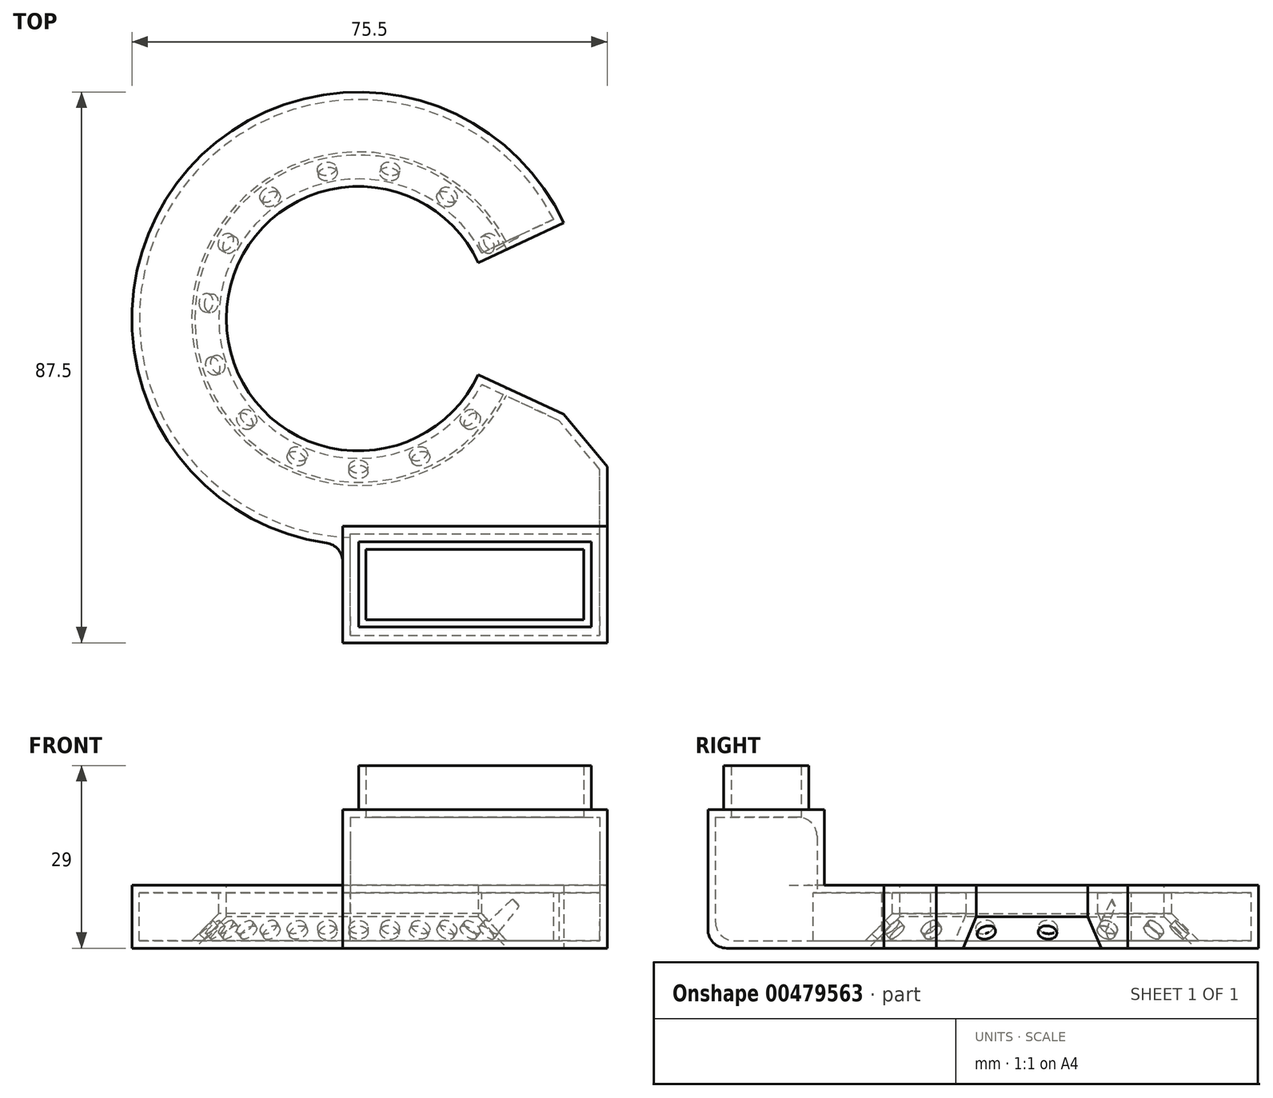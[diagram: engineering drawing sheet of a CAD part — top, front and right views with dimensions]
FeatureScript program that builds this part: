
annotation { "Feature Type Name" : "Feature", "Feature Type Description" : "" }
export const myFeature = defineFeature(function(context is Context, id is Id, definition is map)
    precondition{}
    {
        {
            var Q0;
            Q0=qCreatedBy(makeId("Front.planeOp"),FACE);
            var sketch = newSketch(context, id + "F0", { "sketchPlane" : qUnion([Q0])});
            skLineSegment(sketch, "E0", {"start": v(0, 66.2) * mm, "end": v(0, -56.66) * mm, "construction": true});
            skLineSegment(sketch, "E1", {"start": v(21, 10) * mm, "end": v(36, 10) * mm});
            skLineSegment(sketch, "E2", {"start": v(36, 10) * mm, "end": v(36, 0) * mm});
            skLineSegment(sketch, "E3", {"start": v(36, 0) * mm, "end": v(26, 0) * mm});
            skLineSegment(sketch, "E4", {"start": v(21, 10) * mm, "end": v(21, 5) * mm});
            skLineSegment(sketch, "E5", {"start": v(21, 5) * mm, "end": v(26, 0) * mm});
            skSolve(sketch);
        }
        {
            var Q0;
            Q0=makeQuery(id+"F0.imprint","IMPRINT",FACE,{"disambiguationData":[TD([[makeQuery(id+"F0.imprint","IMPRINT",EDGE,{"derivedFrom":sQuery(id+"F0.wireOp",EDGE,"E1")}),-1.0]])]});
            var Q1;
            Q1=sQuery(id+"F0.wireOp",EDGE,"E0");
            revolve(context, id + "F1", {"entities" : qUnion([Q0]), "axis" : qUnion([Q1]), "revolveType" : RevolveType.TWO_DIRECTIONS, "angle" : 335 * degree, "angleBack" : 25 * degree});
        }
        {
            var Q0;
            Q0=qCreatedBy(makeId("Top.planeOp"),FACE);
            var sketch = newSketch(context, id + "F2", { "sketchPlane" : qUnion([Q0])});
            skLineSegment(sketch, "E6.bottom", {"start": v(-2.5, -51.5) * mm, "end": v(39.5, -51.5) * mm});
            skLineSegment(sketch, "E6.left", {"start": v(-2.5, -51.5) * mm, "end": v(-2.5, -31.44) * mm});
            skLineSegment(sketch, "E6.right", {"start": v(39.5, -51.5) * mm, "end": v(39.5, -23.5) * mm});
            skPoint(sketch, "E7.orphan", {"position": v(23.56, -10.99) * mm});
            skPoint(sketch, "E8.orphan", {"position": v(23.56, 10.99) * mm});
            skPoint(sketch, "E9.0", {"position": v(32.63, -15.21) * mm});
            skLineSegment(sketch, "E10", {"start": v(39.5, -23.5) * mm, "end": v(32.63, -15.21) * mm});
            skLineSegment(sketch, "E11", {"start": v(32.63, -15.21) * mm, "end": v(-2.5, -31.44) * mm});
            skSolve(sketch);
        }
        {
            var Q0;
            Q0=makeQuery(id+"F2.imprint","IMPRINT",FACE,{"disambiguationData":[TD([[makeQuery(id+"F2.imprint","IMPRINT",EDGE,{"derivedFrom":sQuery(id+"F2.wireOp",EDGE,"E6.bottom")}),1.0]])]});
            var Q1;
            Q1=makeQuery(id+"F1.opRevolve","SWEPT_FACE",FACE,{"disambiguationData":[OSD([sQuery(id+"F0.wireOp",EDGE,"E1")])]});
            extrude(context, id + "F3", {"entities" : qUnion([Q0]), "operationType" : NewBodyOperationType.ADD, "endBound" : BoundingType.UP_TO_SURFACE, "endBoundEntityFace" : qUnion([Q1]), "depth" : 25 * mm});
        }
        {
            var Q0;
            {var subQ0=sQuery(id+"F0.wireOp",EDGE,"E1");Q0=makeQuery(id+"F3.boolean.opBoolean","MERGE",FACE,{"derivedFrom":[makeQuery(id+"F1.opRevolve","SWEPT_FACE",FACE,{"disambiguationData":[OSD([subQ0])]}),makeQuery(id+"F3.opExtrude","CAP_FACE",FACE,{"disambiguationData":[OSD([subQ0])],"isStart":false})]});}
            var sketch = newSketch(context, id + "F4", { "sketchPlane" : qUnion([Q0])});
            skPoint(sketch, "E12.0", {"position": v(-2.5, -51.5) * mm});
            skLineSegment(sketch, "E13.bottom", {"start": v(-2.5, -51.5) * mm, "end": v(39.5, -51.5) * mm});
            skLineSegment(sketch, "E13.top", {"start": v(-2.5, -32.96) * mm, "end": v(39.5, -32.96) * mm});
            skLineSegment(sketch, "E13.left", {"start": v(-2.5, -51.5) * mm, "end": v(-2.5, -32.96) * mm});
            skLineSegment(sketch, "E13.right", {"start": v(39.5, -51.5) * mm, "end": v(39.5, -32.96) * mm});
            skSolve(sketch);
        }
        {
            var Q0;
            Q0=makeQuery(id+"F4.imprint","IMPRINT",FACE,{"disambiguationData":[TD([[makeQuery(id+"F4.imprint","IMPRINT",EDGE,{"derivedFrom":sQuery(id+"F4.wireOp",EDGE,"E13.bottom")}),1.0]])]});
            extrude(context, id + "F5", {"entities" : qUnion([Q0]), "operationType" : NewBodyOperationType.ADD, "depth" : 12 * mm});
        }
        {
            var Q0;
            Q0=makeQuery(id+"F5.opExtrude","CAP_FACE",FACE,{"disambiguationData":[OSD([sQuery(id+"F4.wireOp",EDGE,"E13.bottom"),sQuery(id+"F4.wireOp",EDGE,"E13.top"),sQuery(id+"F4.wireOp",EDGE,"E13.left"),sQuery(id+"F4.wireOp",EDGE,"E13.right")])],"isStart":false});
            var sketch = newSketch(context, id + "F6", { "sketchPlane" : qUnion([Q0])});
            skPoint(sketch, "E14.0", {"position": v(-2.5, -32.96) * mm});
            skPoint(sketch, "E15.0", {"position": v(-2.5, -51.5) * mm});
            skPoint(sketch, "E16.0", {"position": v(39.5, -51.5) * mm});
            skPoint(sketch, "E17.0", {"position": v(39.5, -32.96) * mm});
            skLineSegment(sketch, "E18", {"start": v(-2.5, -32.96) * mm, "end": v(39.5, -51.5) * mm, "construction": true});
            skLineSegment(sketch, "E19", {"start": v(-2.5, -51.5) * mm, "end": v(39.5, -32.96) * mm, "construction": true});
            skLineSegment(sketch, "E20.bottom", {"start": v(37, -35.46) * mm, "end": v(0, -35.46) * mm});
            skLineSegment(sketch, "E20.top", {"start": v(37, -49) * mm, "end": v(0, -49) * mm});
            skLineSegment(sketch, "E20.left", {"start": v(37, -35.46) * mm, "end": v(37, -49) * mm});
            skLineSegment(sketch, "E20.right", {"start": v(0, -35.46) * mm, "end": v(0, -49) * mm});
            skPoint(sketch, "E20.middle", {"position": v(18.5, -42.23) * mm});
            skSolve(sketch);
        }
        {
            var Q0;
            Q0=makeQuery(id+"F6.imprint","IMPRINT",FACE,{"disambiguationData":[TD([[makeQuery(id+"F6.imprint","IMPRINT",EDGE,{"derivedFrom":sQuery(id+"F6.wireOp",EDGE,"E20.bottom")}),1.0]])]});
            extrude(context, id + "F7", {"entities" : qUnion([Q0]), "operationType" : NewBodyOperationType.ADD, "depth" : 7 * mm});
        }
        {
            var Q0;
            Q0=makeQuery(id+"F7.opExtrude","CAP_FACE",FACE,{"disambiguationData":[OSD([sQuery(id+"F6.wireOp",EDGE,"E20.bottom"),sQuery(id+"F6.wireOp",EDGE,"E20.top"),sQuery(id+"F6.wireOp",EDGE,"E20.left"),sQuery(id+"F6.wireOp",EDGE,"E20.right")])],"isStart":false});
            shell(context, id + "F8", {"entities" : qUnion([Q0]), "thickness" : 1.2 * mm});
        }
        {
            var Q0;
            Q0=qCreatedBy(makeId("Top.planeOp"),FACE);
            var sketch = newSketch(context, id + "F9", { "sketchPlane" : qUnion([Q0])});
            skLineSegment(sketch, "E21", {"start": v(71.7, 0) * mm, "end": v(-68.59, 0) * mm});
            skSolve(sketch);
        }
        {
            var Q0;
            Q0=sQuery(id+"F9.wireOp",EDGE,"E21");
            cPlane(context, id + "F10", {"entities" : qUnion([Q0]), "cplaneType" : CPlaneType.LINE_ANGLE, "offset" : 25 * mm, "angle" : 45 * degree, "width" : 150 * mm, "height" : 150 * mm});
        }
        {
            var Q0;
            Q0=qCreatedBy(id+"F10.planeOp",FACE);
            var sketch = newSketch(context, id + "F11", { "sketchPlane" : qUnion([Q0])});
            skCircle(sketch, "E22", {"center": v(0, -14.85) * mm, "radius": 1.5 * mm});
            skSolve(sketch);
        }
        {
            var Q0;
            Q0=makeQuery(id+"F11.imprint","IMPRINT",FACE,{"disambiguationData":[TD([[makeQuery(id+"F11.imprint","IMPRINT",EDGE,{"derivedFrom":sQuery(id+"F11.wireOp",EDGE,"E22")}),1.0]])]});
            extrude(context, id + "F12", {"entities" : qUnion([Q0]), "depth" : 25 * mm});
        }
        {
            var Q0;
            Q0=makeQuery(id+"F12.opExtrude","SWEPT_BODY",BODY,{"disambiguationData":[OSD([sQuery(id+"F11.wireOp",EDGE,"E22")])]});
            var Q1;
            Q1=sQuery(id+"F0.wireOp",EDGE,"E0");
            circularPattern(context, id + "F13", {"operationType" : NewBodyOperationType.REMOVE, "entities" : qUnion([Q0]), "axis" : qUnion([Q1]), "angle" : 360 * degree, "instanceCount" : 15, "equalSpace" : true});
        }
        {
            var Q0;
            Q0=makeQuery(id+"F3.opExtrude","CAP_EDGE",EDGE,{"disambiguationData":[OSD([sQuery(id+"F2.wireOp",EDGE,"E6.bottom")])],"isStart":true});
            var Q1;
            Q1=makeQuery(id+"F8.opShell","OFFSET_EDGE",EDGE,{"disambiguationData":[OSD([sQuery(id+"F2.wireOp",EDGE,"E6.bottom")])]});
            var Q2;
            {var subQ0=sQuery(id+"F4.wireOp",EDGE,"E13.top");Q2=makeQuery(id+"F8.opShell","OFFSET_EDGE",EDGE,{"disambiguationData":[OSD([subQ0]),TDD([makeQuery(id+"F5.opExtrude","CAP_EDGE",EDGE,{"disambiguationData":[OSD([subQ0])],"isStart":true})])]});}
            var Q3;
            Q3=makeQuery(id+"F5.opExtrude","CAP_EDGE",EDGE,{"disambiguationData":[OSD([sQuery(id+"F4.wireOp",EDGE,"E13.top")])],"isStart":true});
            var Q4;
            Q4=makeQuery(id+"F3.boolean.opBoolean","INTERSECT",EDGE,{"derivedFrom":[makeQuery(id+"F1.opRevolve","SWEPT_FACE",FACE,{"disambiguationData":[OSD([sQuery(id+"F0.wireOp",EDGE,"E2")])]}),makeQuery(id+"F3.opExtrude","SWEPT_FACE",FACE,{"disambiguationData":[OSD([sQuery(id+"F2.wireOp",EDGE,"E6.left")])]})]});
            var Q5;
            Q5=makeQuery(id+"F3.boolean.opBoolean","INTERSECT",EDGE,{"derivedFrom":[makeQuery(id+"F1.opRevolve","SWEPT_FACE",FACE,{"disambiguationData":[OSD([sQuery(id+"F0.wireOp",EDGE,"E2")])]}),makeQuery(id+"F3.opExtrude","SWEPT_FACE",FACE,{"disambiguationData":[OSD([sQuery(id+"F2.wireOp",EDGE,"E6.right")])]})]});
            fillet(context, id + "F14", {"entities" : qUnion([Q0, Q1, Q2, Q3, Q4, Q5]), "radius" : 3 * mm, "tangentPropagation" : true, "allowEdgeOverflow" : false});
        }
    });
